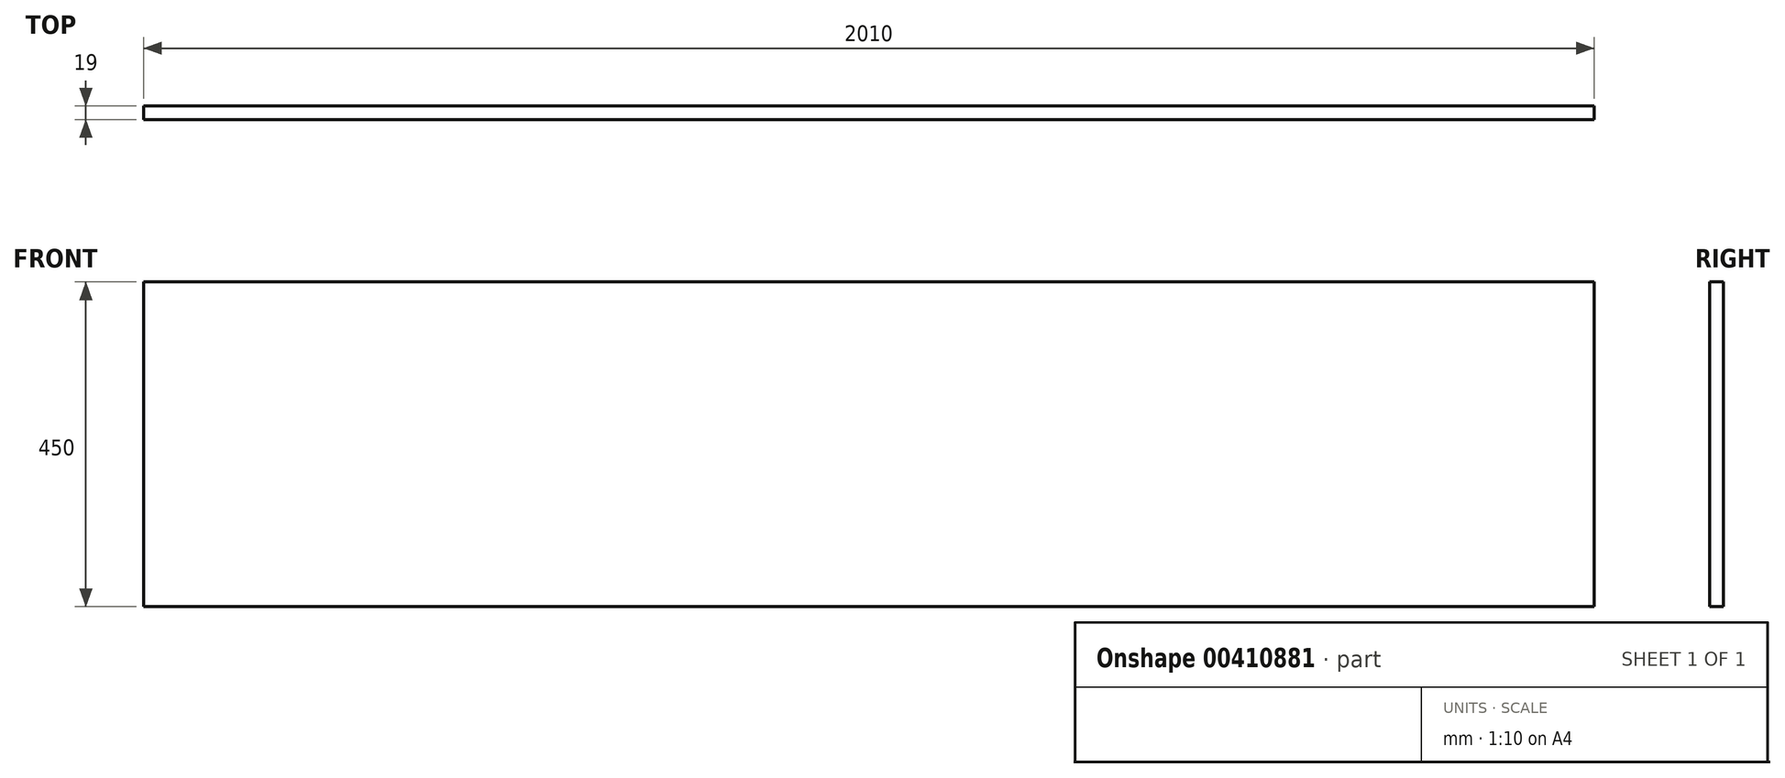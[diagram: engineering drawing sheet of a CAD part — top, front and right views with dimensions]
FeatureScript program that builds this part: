
annotation { "Feature Type Name" : "Feature", "Feature Type Description" : "" }
export const myFeature = defineFeature(function(context is Context, id is Id, definition is map)
    precondition{}
    {
        {
            var Q0;
            Q0=qCreatedBy(makeId("Top.planeOp"),FACE);
            var sketch = newSketch(context, id + "F0", { "sketchPlane" : qUnion([Q0])});
            skLineSegment(sketch, "E0.bottom", {"start": v(-1013.95, 22.5) * mm, "end": v(996.05, 22.5) * mm});
            skLineSegment(sketch, "E0.top", {"start": v(-1013.95, 3.5) * mm, "end": v(996.05, 3.5) * mm});
            skLineSegment(sketch, "E0.left", {"start": v(-1013.95, 22.5) * mm, "end": v(-1013.95, 3.5) * mm});
            skLineSegment(sketch, "E0.right", {"start": v(996.05, 22.5) * mm, "end": v(996.05, 3.5) * mm});
            skSolve(sketch);
        }
        {
            var Q0;
            Q0 = qSketchRegion(id + "F0", true);
            extrude(context, id + "F1", {"entities" : qUnion([Q0]), "depth" : 450 * mm});
        }
    });
